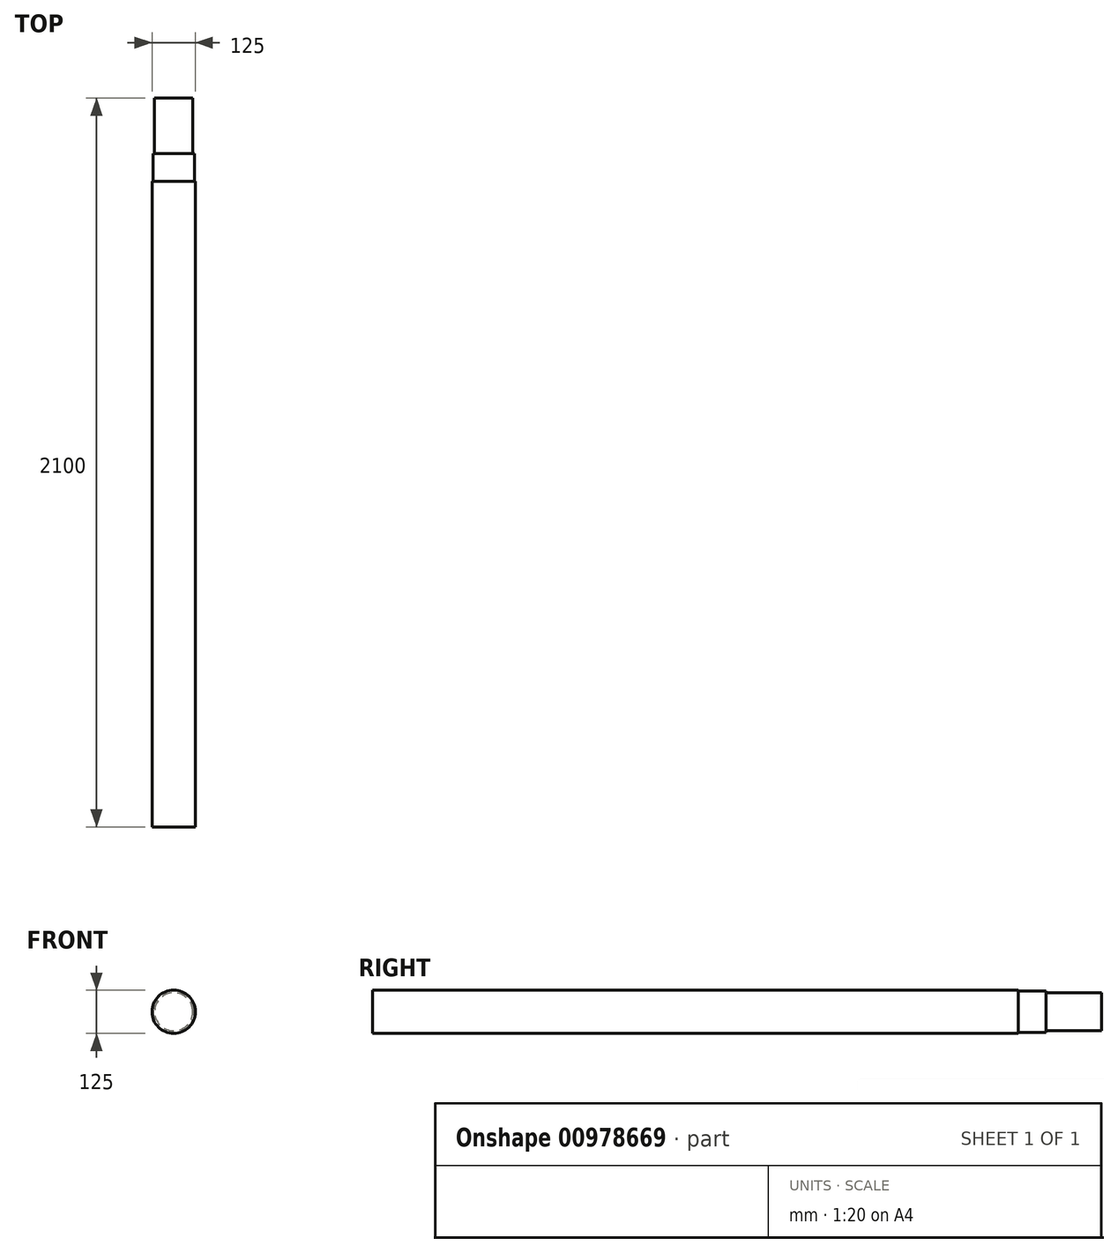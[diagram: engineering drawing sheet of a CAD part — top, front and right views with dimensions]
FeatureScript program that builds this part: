
annotation { "Feature Type Name" : "Feature", "Feature Type Description" : "" }
export const myFeature = defineFeature(function(context is Context, id is Id, definition is map)
    precondition{}
    {
        {
            var Q0;
            Q0=qCreatedBy(makeId("Front.planeOp"),FACE);
            var sketch = newSketch(context, id + "F0", { "sketchPlane" : qUnion([Q0])});
            skCircle(sketch, "E0", {"center": v(0, 0) * mm, "radius": 62.5 * mm});
            skSolve(sketch);
        }
        {
            var Q0;
            Q0=makeQuery(id+"F0.imprint","IMPRINT",FACE,{"disambiguationData":[TD([[makeQuery(id+"F0.imprint","IMPRINT",EDGE,{"derivedFrom":sQuery(id+"F0.wireOp",EDGE,"E0")}),1.0]])]});
            extrude(context, id + "F1", {"entities" : qUnion([Q0]), "depth" : 2100 * mm, "offsetDistance" : 25 * mm, "symmetric" : true});
        }
        {
            var Q0;
            Q0=makeQuery(id+"F1.opExtrude","CAP_FACE",FACE,{"disambiguationData":[OSD([sQuery(id+"F0.wireOp",EDGE,"E0")])],"isStart":true});
            var sketch = newSketch(context, id + "F2", { "sketchPlane" : qUnion([Q0])});
            skCircle(sketch, "E1", {"center": v(0, 0) * mm, "radius": 60 * mm});
            skCircle(sketch, "E2", {"center": v(0, 0) * mm, "radius": 55 * mm});
            skSolve(sketch);
        }
        {
            var Q0;
            Q0=makeQuery(id+"F2.imprint","IMPRINT",FACE,{"disambiguationData":[TD([[makeQuery(id+"F2.imprint","IMPRINT",EDGE,{"derivedFrom":sQuery(id+"F2.wireOp",EDGE,"E1")}),-1.0]])]});
            extrude(context, id + "F3", {"entities" : qUnion([Q0]), "operationType" : NewBodyOperationType.REMOVE, "oppositeDirection" : true, "depth" : 240 * mm, "offsetDistance" : 25 * mm});
        }
        {
            var Q0;
            Q0 = qSketchRegion(id + "F2", true);
            extrude(context, id + "F4", {"entities" : qUnion([Q0]), "operationType" : NewBodyOperationType.REMOVE, "oppositeDirection" : true, "depth" : 160 * mm, "offsetDistance" : 25 * mm});
        }
    });
